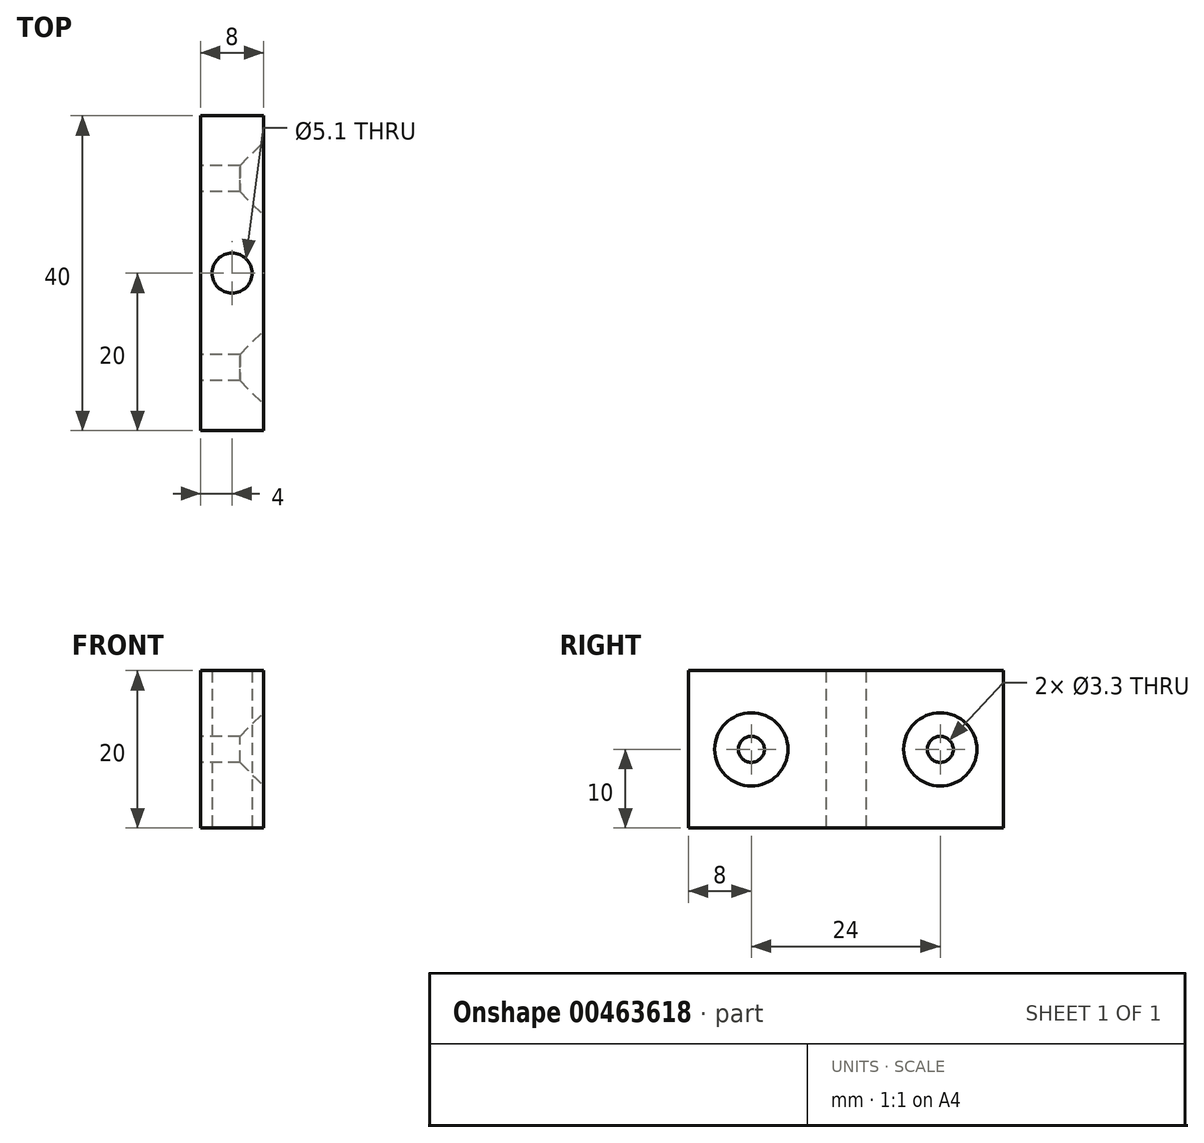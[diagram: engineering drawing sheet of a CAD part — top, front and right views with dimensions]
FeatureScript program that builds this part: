
annotation { "Feature Type Name" : "Feature", "Feature Type Description" : "" }
export const myFeature = defineFeature(function(context is Context, id is Id, definition is map)
    precondition{}
    {
        {
            var Q0;
            Q0=qCreatedBy(makeId("Right.planeOp"),FACE);
            var sketch = newSketch(context, id + "F0", { "sketchPlane" : qUnion([Q0])});
            skLineSegment(sketch, "E0.bottom", {"start": v(-20, 10) * mm, "end": v(20, 10) * mm});
            skLineSegment(sketch, "E0.top", {"start": v(-20, -10) * mm, "end": v(20, -10) * mm});
            skLineSegment(sketch, "E0.left", {"start": v(-20, 10) * mm, "end": v(-20, -10) * mm});
            skLineSegment(sketch, "E0.right", {"start": v(20, 10) * mm, "end": v(20, -10) * mm});
            skPoint(sketch, "E0.middle", {"position": v(0, 0) * mm});
            skCircle(sketch, "E1", {"center": v(-12, 0) * mm, "radius": 1.65 * mm});
            skCircle(sketch, "E2", {"center": v(12, 0) * mm, "radius": 1.65 * mm});
            skSolve(sketch);
        }
        {
            var Q0;
            Q0=makeQuery(id+"F0.imprint","IMPRINT",FACE,{"disambiguationData":[TD([[makeQuery(id+"F0.imprint","IMPRINT",EDGE,{"derivedFrom":sQuery(id+"F0.wireOp",EDGE,"E0.bottom")}),-1.0]])]});
            extrude(context, id + "F1", {"entities" : qUnion([Q0]), "depth" : 8 * mm});
        }
        {
            var Q0;
            Q0=makeQuery(id+"F1.opExtrude","CAP_EDGE",EDGE,{"disambiguationData":[OSD([sQuery(id+"F0.wireOp",EDGE,"E1")])],"isStart":false});
            var Q1;
            Q1=makeQuery(id+"F1.opExtrude","CAP_EDGE",EDGE,{"disambiguationData":[OSD([sQuery(id+"F0.wireOp",EDGE,"E2")])],"isStart":false});
            chamfer(context, id + "F2", {"entities" : qUnion([Q0, Q1]), "width" : 3 * mm, "tangentPropagation" : true});
        }
        {
            var Q0;
            Q0=makeQuery(id+"F1.opExtrude","SWEPT_FACE",FACE,{"disambiguationData":[OSD([sQuery(id+"F0.wireOp",EDGE,"E0.top")])]});
            var sketch = newSketch(context, id + "F3", { "sketchPlane" : qUnion([Q0])});
            skCircle(sketch, "E3", {"center": v(4, 0) * mm, "radius": 2.55 * mm});
            skSolve(sketch);
        }
        {
            var Q0;
            Q0=makeQuery(id+"F3.imprint","IMPRINT",FACE,{"disambiguationData":[TD([[makeQuery(id+"F3.imprint","IMPRINT",EDGE,{"derivedFrom":sQuery(id+"F3.wireOp",EDGE,"E3")}),1.0]])]});
            extrude(context, id + "F4", {"entities" : qUnion([Q0]), "operationType" : NewBodyOperationType.REMOVE, "endBound" : BoundingType.THROUGH_ALL, "oppositeDirection" : true, "depth" : 25 * mm});
        }
    });
